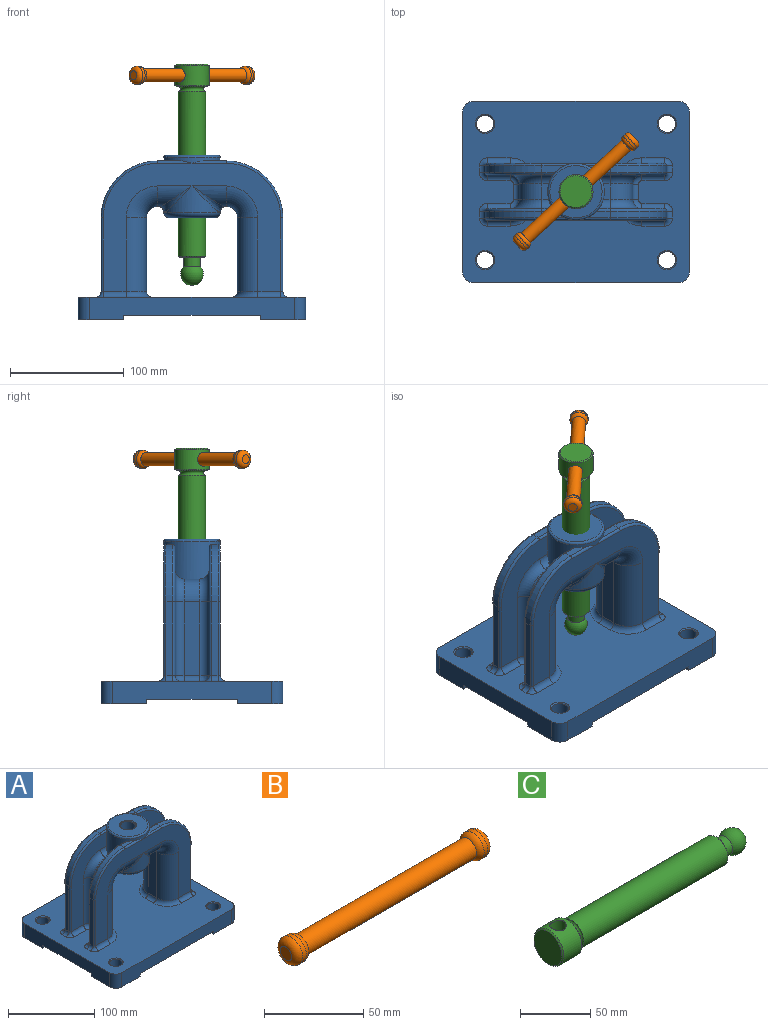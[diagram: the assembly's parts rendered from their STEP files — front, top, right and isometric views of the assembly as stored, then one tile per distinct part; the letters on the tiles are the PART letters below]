
ASSEMBLY  parts=3 mates=2
PART A: 158 faces, bbox 200x160x145 mm
  f0: plane 7x0.83mm, normal (0,0,-1), area 1.9mm2, adj f12,f54,f150
  f1: plane 7x0.83mm, normal (0,0,-1), area 1.9mm2, adj f15,f109,f153
  f2: cylinder r=25mm len=48.62mm, axis (0,0,-1), area 569.9mm2, adj f148,f151,f154
  f3: plane 14x6mm, normal (0,0,1), area 74.6mm2, adj f5,f22,f48,f144
  f4: cylinder r=8mm len=10mm, axis (1,0,0), area 104.3mm2, adj f24,f44,f104,f144
  f5: cylinder r=8mm len=10mm, axis (1,0,0), area 104.3mm2, adj f3,f23,f49,f144
  f6: cylinder r=2mm len=11.67mm, axis (1,0,0), area 33.2mm2, adj f8,f23,f50,f144
  f7: cylinder r=2mm len=11.67mm, axis (1,0,0), area 33.2mm2, adj f24,f45,f105,f144
  f8: plane 20.2x6mm, normal (0,0,1), area 91.8mm2, adj f6,f9,f51,f144
  f9: cylinder r=2mm len=30mm, axis (1,0,0), area 77.9mm2, adj f8,f52,f65,f144
  f10: cylinder r=2mm len=30mm, axis (1,0,0), area 77.9mm2, adj f45,f65,f107,f144
  f11: cylinder r=18mm len=30mm, axis (1,0,0), area 354.8mm2, adj f46,f65,f108,f154
  f12: cylinder r=18mm len=30mm, axis (1,0,0), area 354.8mm2, adj f0,f53,f65,f148
  f13: plane 7x0.83mm, normal (0,0,-1), area 1.9mm2, adj f14,f54,f150
  f14: cylinder r=18mm len=30mm, axis (1,0,0), area 354.8mm2, adj f13,f55,f69,f149
  f15: cylinder r=18mm len=30mm, axis (1,0,0), area 354.8mm2, adj f1,f69,f110,f152
  f16: cylinder r=2mm len=30mm, axis (1,0,0), area 77.9mm2, adj f18,f69,f111,f144
  f17: cylinder r=2mm len=30mm, axis (1,0,0), area 77.9mm2, adj f47,f56,f69,f144
  f18: plane 20.2x6mm, normal (0,0,1), area 91.8mm2, adj f16,f20,f112,f144
  f19: cylinder r=2mm len=11.67mm, axis (1,0,0), area 33.2mm2, adj f26,f47,f58,f144
  f20: cylinder r=2mm len=11.67mm, axis (1,0,0), area 33.2mm2, adj f18,f25,f113,f144
  f21: cylinder r=8mm len=10mm, axis (1,0,0), area 104.3mm2, adj f25,f44,f114,f144
  f22: cylinder r=8mm len=10mm, axis (1,0,0), area 104.3mm2, adj f3,f26,f59,f144
  f23: plane 113x58mm, normal (0,-1,0), area 2693.8mm2, adj f5,f6,f49,f50,f61,f62,f89,f144
  f24: plane 113x58mm, normal (0,-1,0), area 2693.8mm2, adj f4,f7,f104,f105,f116,f117,f142,f144
  f25: plane 113x58mm, normal (0,1,0), area 2693.8mm2, adj f20,f21,f113,f114,f125,f126,f135,f144
  f26: plane 113x58mm, normal (0,1,0), area 2693.8mm2, adj f19,f22,f58,f59,f72,f73,f82,f144
  f27: plane 200x160mm, normal (0,0,-1), area 25600mm2, adj f28,f30,f31,f36,f37,f39,f40,f90
  f28: plane 140x20mm, normal (-1,0,0), area 2480mm2, adj f27,f29,f32,f35,f37,f38,f40,f41
  f29: cylinder r=10mm len=20mm, axis (0,0,-1), area 314.2mm2, adj f28,f30,f35,f41
  f30: plane 180x20mm, normal (0,-1,0), area 3120mm2, adj f27,f29,f35,f39,f41,f91,f98,f100
  f31: plane 180x20mm, normal (0,1,0), area 3120mm2, adj f27,f32,f35,f36,f38,f92,f95,f97
  f32: cylinder r=10mm len=20mm, axis (0,0,-1), area 314.2mm2, adj f28,f31,f35,f38
  f33: cylinder r=7.5mm len=19mm, axis (0,0,-1), area 895.4mm2, adj f38,f43
  f34: cylinder r=7.5mm len=19mm, axis (0,0,-1), area 895.4mm2, adj f41,f42
  f35: plane 200x160mm, normal (0,0,1), area 26736.7mm2, adj f28,f29,f30,f31,f32,f42,f43,f74
  f36: plane 40x4mm, normal (1,0,0), area 160mm2, adj f27,f31,f37,f38
  f37: plane 40x4mm, normal (0,-1,0), area 160mm2, adj f27,f28,f36,f38
  f38: plane 40x40mm, normal (0,0,-1), area 1401.8mm2, adj f28,f31,f32,f33,f36,f37
  f39: plane 40x4mm, normal (1,0,0), area 160mm2, adj f27,f30,f40,f41
  f40: plane 40x4mm, normal (0,1,0), area 160mm2, adj f27,f28,f39,f41
  f41: plane 40x40mm, normal (0,0,-1), area 1401.8mm2, adj f28,f29,f30,f34,f39,f40
  f42: cone r=7.5mm half-angle=45deg, axis (0,0,1), area 71.1mm2, adj f34,f35
  f43: cone r=7.5mm half-angle=45deg, axis (0,0,1), area 71.1mm2, adj f33,f35
  f44: plane 14x6mm, normal (0,0,1), area 74.6mm2, adj f4,f21,f103,f144
  f45: plane 20.2x6mm, normal (0,0,1), area 91.8mm2, adj f7,f10,f106,f144
  f46: plane 7x0.83mm, normal (0,0,-1), area 1.9mm2, adj f11,f109,f153
  f47: plane 20.2x6mm, normal (0,0,1), area 91.8mm2, adj f17,f19,f57,f144
  f48: cylinder r=20mm len=20mm, axis (0,1,0), area 439.8mm2, adj f3,f49,f59,f60
  f49: torus R=28mm, axis (0,1,0), area 452.2mm2, adj f5,f23,f48,f61
  f50: torus R=48mm, axis (0,1,0), area 243.2mm2, adj f6,f23,f51,f62
  f51: cylinder r=50mm len=50mm, axis (0,1,0), area 471.2mm2, adj f8,f50,f52,f63
  f52: torus R=48mm, axis (0,1,0), area 243.2mm2, adj f9,f51,f64,f65
  f53: torus R=28mm, axis (0,1,0), area 734.6mm2, adj f12,f54,f65,f66
  f54: cylinder r=10mm len=14mm, axis (0,1,0), area 219.9mm2, adj f0,f13,f53,f55,f67
  f55: torus R=28mm, axis (0,1,0), area 734.6mm2, adj f14,f54,f68,f69
  f56: torus R=48mm, axis (0,1,0), area 243.2mm2, adj f17,f57,f69,f70
  f57: cylinder r=50mm len=50mm, axis (0,1,0), area 471.2mm2, adj f47,f56,f58,f71
  f58: torus R=48mm, axis (0,1,0), area 243.2mm2, adj f19,f26,f57,f72
  f59: torus R=28mm, axis (0,1,0), area 452.2mm2, adj f22,f26,f48,f73
  f60: plane 65x14mm, normal (-1,0,0), area 910mm2, adj f48,f61,f73,f86
  f61: cylinder r=8mm len=65mm, axis (0,0,1), area 816.8mm2, adj f23,f49,f60,f88
  f62: cylinder r=2mm len=65mm, axis (0,0,1), area 204.2mm2, adj f23,f50,f63,f87
  f63: plane 65x6mm, normal (-1,0,0), area 390mm2, adj f51,f62,f64,f85
  f64: cylinder r=2mm len=65mm, axis (0,0,1), area 204.2mm2, adj f52,f63,f65,f83
  f65: plane 156x113mm, normal (0,1,0), area 6187.6mm2, adj f9,f10,f11,f12,f52,f53,f64,f66
  f66: cylinder r=18mm len=65mm, axis (0,0,1), area 1837.8mm2, adj f53,f65,f67,f79
  f67: plane 65x14mm, normal (1,0,0), area 910mm2, adj f54,f66,f68,f77
  f68: cylinder r=18mm len=65mm, axis (0,0,1), area 1837.8mm2, adj f55,f67,f69,f75
  f69: plane 156x113mm, normal (0,-1,0), area 6187.6mm2, adj f14,f15,f16,f17,f55,f56,f68,f70
  f70: cylinder r=2mm len=65mm, axis (0,0,1), area 204.2mm2, adj f56,f69,f71,f76
  f71: plane 65x6mm, normal (-1,0,0), area 390mm2, adj f57,f70,f72,f78
  f72: cylinder r=2mm len=65mm, axis (0,0,1), area 204.2mm2, adj f26,f58,f71,f80
  f73: cylinder r=8mm len=65mm, axis (0,0,1), area 816.8mm2, adj f26,f59,f60,f84
  f74: cylinder r=5mm len=20mm, axis (-1,0,0), area 157.1mm2, adj f35,f69,f75,f76
  f75: torus R=23mm, axis (0,0,1), area 244.5mm2, adj f35,f68,f74,f77
  f76: torus R=7mm, axis (0,0,1), area 47.1mm2, adj f35,f70,f74,f78
  f77: cylinder r=5mm len=14mm, axis (0,-1,0), area 110mm2, adj f35,f67,f75,f79
  f78: cylinder r=5mm len=6mm, axis (0,1,0), area 47.1mm2, adj f35,f71,f76,f80
  f79: torus R=23mm, axis (0,0,1), area 244.5mm2, adj f35,f66,f77,f81
  f80: torus R=7mm, axis (0,0,1), area 47.1mm2, adj f35,f72,f78,f82
  f81: cylinder r=5mm len=20mm, axis (1,0,0), area 157.1mm2, adj f35,f65,f79,f83
  f82: cylinder r=5mm len=20mm, axis (1,0,0), area 157.1mm2, adj f26,f35,f80,f84
  f83: torus R=7mm, axis (0,0,1), area 47.1mm2, adj f35,f64,f81,f85
  f84: torus R=3mm, axis (0,0,1), area 76.3mm2, adj f35,f73,f82,f86
  f85: cylinder r=5mm len=6mm, axis (0,1,0), area 47.1mm2, adj f35,f63,f83,f87
  f86: cylinder r=5mm len=14mm, axis (0,1,0), area 110mm2, adj f35,f60,f84,f88
  f87: torus R=7mm, axis (0,0,1), area 47.1mm2, adj f35,f62,f85,f89
  f88: torus R=3mm, axis (0,0,1), area 76.3mm2, adj f35,f61,f86,f89
  f89: cylinder r=5mm len=20mm, axis (-1,0,0), area 157.1mm2, adj f23,f35,f87,f88
  f90: plane 140x20mm, normal (1,0,0), area 2480mm2, adj f27,f35,f91,f92,f96,f97,f99,f100
  f91: cylinder r=10mm len=20mm, axis (0,0,-1), area 314.2mm2, adj f30,f35,f90,f100
  f92: cylinder r=10mm len=20mm, axis (0,0,-1), area 314.2mm2, adj f31,f35,f90,f97
  f93: cylinder r=7.5mm len=19mm, axis (0,0,-1), area 895.4mm2, adj f97,f102
  f94: cylinder r=7.5mm len=19mm, axis (0,0,-1), area 895.4mm2, adj f100,f101
  f95: plane 40x4mm, normal (-1,0,0), area 160mm2, adj f27,f31,f96,f97
  f96: plane 40x4mm, normal (0,-1,0), area 160mm2, adj f27,f90,f95,f97
  f97: plane 40x40mm, normal (0,0,-1), area 1401.8mm2, adj f31,f90,f92,f93,f95,f96
  f98: plane 40x4mm, normal (-1,0,0), area 160mm2, adj f27,f30,f99,f100
  f99: plane 40x4mm, normal (0,1,0), area 160mm2, adj f27,f90,f98,f100
  f100: plane 40x40mm, normal (0,0,-1), area 1401.8mm2, adj f30,f90,f91,f94,f98,f99
  f101: cone r=7.5mm half-angle=45deg, axis (0,0,1), area 71.1mm2, adj f35,f94
  f102: cone r=7.5mm half-angle=45deg, axis (0,0,1), area 71.1mm2, adj f35,f93
  f103: cylinder r=20mm len=20mm, axis (0,1,0), area 439.8mm2, adj f44,f104,f114,f115
  f104: torus R=28mm, axis (0,1,0), area 452.2mm2, adj f4,f24,f103,f116
  f105: torus R=48mm, axis (0,1,0), area 243.2mm2, adj f7,f24,f106,f117
  f106: cylinder r=50mm len=50mm, axis (0,1,0), area 471.2mm2, adj f45,f105,f107,f118
  f107: torus R=48mm, axis (0,1,0), area 243.2mm2, adj f10,f65,f106,f119
  f108: torus R=28mm, axis (0,1,0), area 734.6mm2, adj f11,f65,f109,f120
  f109: cylinder r=10mm len=14mm, axis (0,1,0), area 219.9mm2, adj f1,f46,f108,f110,f121
  f110: torus R=28mm, axis (0,1,0), area 734.6mm2, adj f15,f69,f109,f122
  f111: torus R=48mm, axis (0,1,0), area 243.2mm2, adj f16,f69,f112,f123
  f112: cylinder r=50mm len=50mm, axis (0,1,0), area 471.2mm2, adj f18,f111,f113,f124
  f113: torus R=48mm, axis (0,1,0), area 243.2mm2, adj f20,f25,f112,f125
  f114: torus R=28mm, axis (0,1,0), area 452.2mm2, adj f21,f25,f103,f126
  f115: plane 65x14mm, normal (1,0,0), area 910mm2, adj f103,f116,f126,f139
  f116: cylinder r=8mm len=65mm, axis (0,0,1), area 816.8mm2, adj f24,f104,f115,f141
  f117: cylinder r=2mm len=65mm, axis (0,0,1), area 204.2mm2, adj f24,f105,f118,f140
  f118: plane 65x6mm, normal (1,0,0), area 390mm2, adj f106,f117,f119,f138
  f119: cylinder r=2mm len=65mm, axis (0,0,1), area 204.2mm2, adj f65,f107,f118,f136
  f120: cylinder r=18mm len=65mm, axis (0,0,1), area 1837.8mm2, adj f65,f108,f121,f132
  f121: plane 65x14mm, normal (-1,0,0), area 910mm2, adj f109,f120,f122,f130
  f122: cylinder r=18mm len=65mm, axis (0,0,1), area 1837.8mm2, adj f69,f110,f121,f128
  f123: cylinder r=2mm len=65mm, axis (0,0,1), area 204.2mm2, adj f69,f111,f124,f129
  f124: plane 65x6mm, normal (1,0,0), area 390mm2, adj f112,f123,f125,f131
  f125: cylinder r=2mm len=65mm, axis (0,0,1), area 204.2mm2, adj f25,f113,f124,f133
  f126: cylinder r=8mm len=65mm, axis (0,0,1), area 816.8mm2, adj f25,f114,f115,f137
  f127: cylinder r=5mm len=20mm, axis (1,0,0), area 157.1mm2, adj f35,f69,f128,f129
  f128: torus R=23mm, axis (0,0,1), area 244.5mm2, adj f35,f122,f127,f130
  f129: torus R=7mm, axis (0,0,1), area 47.1mm2, adj f35,f123,f127,f131
  f130: cylinder r=5mm len=14mm, axis (0,-1,0), area 110mm2, adj f35,f121,f128,f132
  f131: cylinder r=5mm len=6mm, axis (0,1,0), area 47.1mm2, adj f35,f124,f129,f133
  f132: torus R=23mm, axis (0,0,1), area 244.5mm2, adj f35,f120,f130,f134
  f133: torus R=7mm, axis (0,0,1), area 47.1mm2, adj f35,f125,f131,f135
  f134: cylinder r=5mm len=20mm, axis (-1,0,0), area 157.1mm2, adj f35,f65,f132,f136
  f135: cylinder r=5mm len=20mm, axis (-1,0,0), area 157.1mm2, adj f25,f35,f133,f137
  f136: torus R=7mm, axis (0,0,1), area 47.1mm2, adj f35,f119,f134,f138
  f137: torus R=3mm, axis (0,0,1), area 76.3mm2, adj f35,f126,f135,f139
  f138: cylinder r=5mm len=6mm, axis (0,1,0), area 47.1mm2, adj f35,f118,f136,f140
  f139: cylinder r=5mm len=14mm, axis (0,1,0), area 110mm2, adj f35,f115,f137,f141
  f140: torus R=7mm, axis (0,0,1), area 47.1mm2, adj f35,f117,f138,f142
  f141: torus R=3mm, axis (0,0,1), area 76.3mm2, adj f35,f116,f139,f142
  f142: cylinder r=5mm len=20mm, axis (1,0,0), area 157.1mm2, adj f24,f35,f140,f141
  f143: plane 46x46mm, normal (0,0,1), area 1363.3mm2, adj f147,f157
  f144: cylinder r=25mm len=50mm, axis (0,0,-1), area 2372.4mm2, adj f3,f4,f5,f6,f7,f8,f9,f10
  f145: cylinder r=25mm len=48.62mm, axis (0,0,-1), area 569.9mm2, adj f149,f151,f152
  f146: plane 40x40mm, normal (0,0,-1), area 958mm2, adj f151,f156
  f147: torus R=23mm, axis (0,0,1), area 479.1mm2, adj f143,f144
  f148: bspline ~29.89x23mm, area 170.7mm2, adj f2,f12,f150
  f149: bspline ~29.89x23mm, area 170.7mm2, adj f14,f145,f150
  f150: torus R=30mm, axis (0,0,-1), area 99.2mm2, adj f0,f13,f148,f149,f151
  f151: torus R=20mm, axis (0,0,1), area 1144mm2, adj f2,f145,f146,f150,f153
  f152: bspline ~29.89x23mm, area 170.7mm2, adj f15,f145,f153
  f153: torus R=30mm, axis (0,0,-1), area 99.2mm2, adj f1,f46,f151,f152,f154
  f154: bspline ~29.89x23mm, area 170.7mm2, adj f2,f11,f153
  f155: cylinder r=8.75mm len=53mm, axis (0,0,1), area 2913.8mm2, adj f156,f157
  f156: cone r=9.75mm half-angle=45deg, axis (0,0,-1), area 82.2mm2, adj f146,f155
  f157: cone r=8.75mm half-angle=45deg, axis (0,0,1), area 82.2mm2, adj f143,f155
PART B: 9 faces, bbox 140x17.3x17.3 mm
  f0: cylinder r=6mm len=120mm, axis (-1,0,0), area 4523.9mm2, adj f1,f5
  f1: torus R=4mm, axis (-1,0,0), area 192.3mm2, adj f0,f2
  f2: cylinder r=8mm len=16mm, axis (-1,0,0), area 127.5mm2, adj f1,f3
  f3: torus R=4mm, axis (-1,0,0), area 258.4mm2, adj f2,f4
  f4: plane 8x8mm, normal (-1,0,0), area 50.3mm2, adj f3
  f5: torus R=4mm, axis (1,0,0), area 192.3mm2, adj f0,f6
  f6: cylinder r=8mm len=16mm, axis (1,0,0), area 127.5mm2, adj f5,f7
  f7: torus R=4mm, axis (1,0,0), area 258.4mm2, adj f6,f8
  f8: plane 8x8mm, normal (1,0,0), area 50.3mm2, adj f7
PART C: 12 faces, bbox 195x30x30 mm
  f0: sphere r=10mm, area 1043.9mm2, adj f1
  f1: cylinder r=7.5mm len=15mm, axis (-1,0,0), area 395.2mm2, adj f0,f2
  f2: plane 22x22mm, normal (1,0,0), area 203.4mm2, adj f1,f8
  f3: cylinder r=12mm len=145mm, axis (-1,0,0), area 10932.7mm2, adj f4,f8
  f4: torus R=12mm, axis (-1,0,0), area 423.5mm2, adj f3,f5
  f5: plane 28x28mm, normal (1,0,0), area 163.4mm2, adj f4,f10
  f6: cylinder r=15mm len=30mm, axis (-1,0,0), area 1457.9mm2, adj f9,f10,f11
  f7: plane 28x28mm, normal (-1,0,0), area 615.8mm2, adj f9
  f8: cone r=12mm half-angle=45deg, axis (-1,0,0), area 102.2mm2, adj f2,f3
  f9: cone r=14mm half-angle=45deg, axis (1,0,0), area 128.8mm2, adj f6,f7
  f10: cone r=15mm half-angle=45deg, axis (-1,0,0), area 128.8mm2, adj f5,f6
  f11: cylinder r=6.1mm len=30mm, axis (0,0,1), area 1100.7mm2, adj f6
PLACE A t=(-36.98,0.37,-64.9)mm fixed
PLACE B rot(axis=(0,0,-1),137.4deg) t=(-36.98,0.37,150.43)mm
PLACE C rot(axis=(0.68,0.27,-0.68),150.2deg) t=(-36.98,0.37,140.43)mm
MATE cylindrical C.f1 <-> A.f2  axis (0,0,-1) through (-36.98,0.37,-9.57)mm
MATE fastened B.f0 <-> C.f11  axis (0.74,0.68,0) through (-36.98,0.37,150.43)mm
